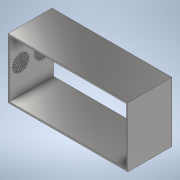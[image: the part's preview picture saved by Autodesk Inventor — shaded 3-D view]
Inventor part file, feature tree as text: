
AUTODESK INVENTOR PART (.ipt)
format: ipt  version: 2021 (Build 250183000, 183)  size: 791,552 bytes
history: native  units: mm
features: extrude x3, sketch x3, other x1, chamfer x1
ambient origin geometry x8: Origin, YZ Plane, XZ Plane, XY Plane, X Axis, Y Axis, Z Axis, Center Point
bodies: Body1 (feature_tree)
feature tree (8):
  other  "Sólido1"
  extrude  "Extrusão1"  Depth=600.0mm
  extrude  "Extrusão2"  Depth=284.0mm
  extrude  "Extrusão3"  Depth=2.0mm
  chamfer  "Chanfro1"  Distance=55.0mm
  sketch  "Esboço2"  dims[d0=300.0mm d1=600.0mm]
  sketch  "Esboço3"  dims[d2=584.0mm d3=284.0mm]
  sketch  "Esboço4"  dims[d4=220.0mm d5=0.0mm d8=150.0mm d11=55.0mm d15=10.0mm d17=10.0mm d18=90.0mm d20=5.0mm d22=50.0mm d24=360.0deg d26=100.0mm d28=360.0deg d30=150.0mm d32=360.0deg d34=200.0mm d36=360.0deg d38=250.0mm d40=360.0deg d42=300.0mm d44=360.0deg d46=350.0mm d48=360.0deg d50=400.0mm d52=360.0deg d54=10.0mm d55=0.0mm d56=500.0mm d57=292.0mm d58=4.0mm d59=4.0mm d60=4.0mm d61=4.0mm d62=4.0mm d63=4.0mm d64=30.0mm d65=0.0mm d66=1.0mm d67=2.0mm d68=45.0deg]
